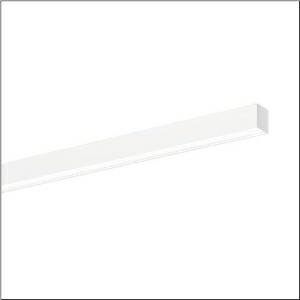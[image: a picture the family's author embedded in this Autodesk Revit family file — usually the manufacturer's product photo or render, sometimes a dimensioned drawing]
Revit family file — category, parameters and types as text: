
# Revit family: silica_r__21_51mx20db42wb_d1f2
name_source: partatom
category: Lighting Fixtures
units: mm (PartAtom-declared; Revit-internal decimal feet)

## family parameters
Cut with Voids When Loaded = No
Host = Face
Light Source = No
Part Type = Normal
Room Calculation Point = No
Round Connector Dimension = Use Diameter
Shared = No

## types (1)
- --- (1 x LED, 3000 lm, 19 W, 4000K)
    Apparent Load = 19 VA
    CIE Flux Codes = 48 79 96 100 100
    Color Rendering = 80
    Color Temperature = 4000K
    Default Elevation = 1800 mm
    Description = Silica® 21, office luminaire, primary optical cover: cover, of PMMA, opal, light emission: direct distribution, primary light characteristic: symmetric, installation type: surface-mounted, LED, rated luminous flux: 3.000lm, luminous efficacy: 158lm/W, light colour: 840, colour temperature: 4000K, control gear: DALI 2, with terminal, 3+2-pole, max. 2.5mm², mains connection: 220..240V, AC, 50/60Hz, rated input power: 19W, luminaire housing, of aluminium, traffic white (RAL 9016), length: 1.504mm, width: 53mm, height: 53mm, protection rating (complete): IP20, insulation class (complete): insulation class I (protective earthing), certification: CE, permissible operating ambient temperature: 0..+35°C, standard: EN 50419, packaging unit: 1 piece
    Height = 53 mm
    Lamp = 1 x LED
    Lamp Light Flux = 3000 lm
    Lamp Power = 19 W
    Lamp count = 1
    Length = 1504 mm
    Luminous efficacy = 158 lm/W
    Manufacturer = Siteco
    ModVariant = No
    Model = 51MX20DB42WB
    Mounting Place = Ceiling
    Mounting Type = Surface mounted
    Number of Poles = 1
    OnlyDefault = Yes
    Power Factor = 1
    Product Name = Silica® 21
    Product group = office luminaire | ceiling mounted
    ProductGroupID = 302
    Protection Class = Protection class I
    Protection Degree = IP 20
    RLX_Detail_Level = 1
    RLX_Emergency_Light_Flux = 0 lm
    RLX_Emergency_Type = 0
    RLX_Emergency_Type_DB = No
    RlxData = <blob elided: 23833 chars, md5=003f242d>
    Socket = socket
    Standby Power = 0 W
    System Light Flux = 3000 lm
    System Power = 19 W
    Type Comments = factory setting: luminous flux: 100 % | dim-lin: 254 | 218 mA
    Type Image = l_1335877.jpg
    URL = http://relux.com
    VarID = @adj_118170
    Voltage = 0 V
    Weight = 0.00 kg
    Width = 53 mm

## geometry (parser evidence)
native form markers: Blend x4, Sweep x10
no freeform markers — native parametric forms only
